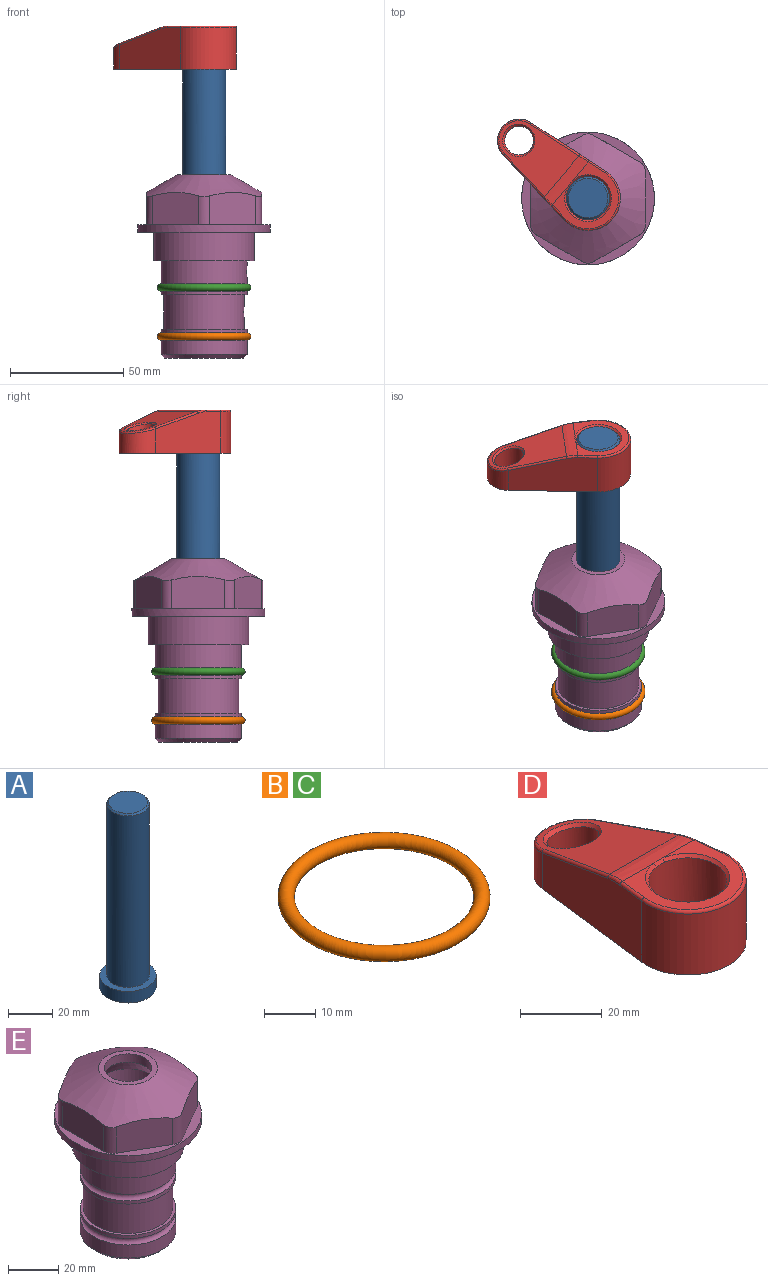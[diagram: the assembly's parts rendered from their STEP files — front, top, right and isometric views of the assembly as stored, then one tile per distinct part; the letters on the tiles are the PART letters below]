
ASSEMBLY  parts=5 mates=4
PART A: 6 faces, bbox 25.4x25.4x101.6 mm
  f0: plane 17.46x17.46mm, normal (0,0,1), area 239.5mm2, adj f5
  f1: plane 25.4x25.4mm, normal (0,0,-1), area 506.7mm2, adj f2
  f2: cylinder r=12.7mm len=25.4mm, axis (0,0,1), area 506.7mm2, adj f1,f3
  f3: plane 25.4x25.4mm, normal (0,0,1), area 221.7mm2, adj f2,f4
  f4: cylinder r=9.53mm len=94.46mm, axis (0,0,1), area 5653mm2, adj f3,f5
  f5: cone r=8.73mm half-angle=45deg, axis (0,0,-1), area 64.4mm2, adj f0,f4
PART B: 1 faces, bbox 44.7x44.7x3.2 mm
  f0: torus R=19.05mm, axis (0,0,1), area 1193.9mm2
PART C: same geometry as B
PART D: 31 faces, bbox 31.7x65.5x19.8 mm
  f0: plane 39.12x18.26mm, normal (0.99,0.12,0), area 612.2mm2, adj f1,f4,f7,f11,f13,f15
  f1: cylinder r=9.53mm len=18.91mm, axis (0,0,-1), area 296.1mm2, adj f0,f2,f7,f17
  f2: plane 39.12x18.26mm, normal (-0.99,0.12,0), area 612.2mm2, adj f1,f4,f7,f12,f14,f16
  f3: cylinder r=6.35mm len=12.7mm, axis (0,0,-1), area 362.4mm2, adj f7,f18
  f4: cylinder r=14.29mm len=28.58mm, axis (0,0,-1), area 882.2mm2, adj f0,f2,f7,f10
  f5: cylinder r=9.53mm len=19.05mm, axis (0,0,-1), area 1092.6mm2, adj f7,f19,f20
  f6: plane 26.99x23.69mm, normal (0,0,1), area 216.2mm2, adj f9,f10,f11,f12,f19
  f7: plane 63.5x28.58mm, normal (0,0,-1), area 661.8mm2, adj f0,f1,f2,f3,f4,f5,f22,f23
  f8: plane 33.52x23.6mm, normal (0,0.26,0.97), area 486mm2, adj f9,f15,f16,f17,f18
  f9: cylinder r=19.05mm len=24.72mm, axis (1,0,0), area 120.4mm2, adj f6,f8,f13,f14,f20
  f10: torus R=13.49mm, axis (0,0,1), area 59mm2, adj f4,f6,f11,f12
  f11: cylinder r=0.79mm len=8.67mm, axis (0.12,-0.99,0), area 10.8mm2, adj f0,f6,f10,f13
  f12: cylinder r=0.79mm len=8.67mm, axis (0.12,0.99,0), area 10.8mm2, adj f2,f6,f10,f14
  f13: bspline ~4.95x1.42mm, area 6.1mm2, adj f0,f9,f11,f15
  f14: bspline ~4.95x1.42mm, area 6.1mm2, adj f2,f9,f12,f16
  f15: cylinder r=0.79mm len=25.95mm, axis (0.12,-0.96,0.26), area 32.9mm2, adj f0,f8,f13,f17
  f16: cylinder r=0.79mm len=25.95mm, axis (0.12,0.96,-0.26), area 32.9mm2, adj f2,f8,f14,f17
  f17: bspline ~18.91x8.38mm, area 30mm2, adj f1,f8,f15,f16
  f18: bspline ~14.29x14.29mm, area 48.3mm2, adj f3,f8
  f19: cone r=9.53mm half-angle=45deg, axis (0,0,1), area 66.5mm2, adj f5,f6,f20
  f20: bspline ~3.22x0.96mm, area 3.5mm2, adj f5,f9,f19
  f21: plane 2.75x2.72mm, normal (0,0,-1), area 2.9mm2, adj f23,f25,f28
  f22: plane 23.05x15.88mm, normal (-0.99,-0.12,0), area 323.6mm2, adj f7,f25,f26,f27,f28,f29
  f23: plane 23.05x15.88mm, normal (0.99,-0.12,0), area 323.6mm2, adj f7,f21,f25,f27,f28,f30
  f24: cylinder r=9.53mm len=10.69mm, axis (0,0,-1), area 114.7mm2, adj f7,f27,f29,f30
  f25: cylinder r=12.7mm len=20.59mm, axis (0,0,-1), area 381.1mm2, adj f7,f21,f22,f23,f26,f28
  f26: plane 2.75x2.72mm, normal (0,0,-1), area 2.9mm2, adj f22,f25,f28
  f27: plane 19.72x18.37mm, normal (0,-0.26,-0.97), area 291.8mm2, adj f22,f23,f24,f28,f29,f30
  f28: cylinder r=15.88mm len=19.92mm, axis (1,0,0), area 54.8mm2, adj f21,f22,f23,f25,f26,f27
  f29: cylinder r=1.59mm len=11mm, axis (0,0,-1), area 34.7mm2, adj f7,f22,f24,f27
  f30: cylinder r=1.59mm len=11mm, axis (0,0,-1), area 34.7mm2, adj f7,f23,f24,f27
PART E: 36 faces, bbox 58.7x58.7x81 mm
  f0: cylinder r=17.78mm len=35.56mm, axis (0,0,1), area 1670.8mm2, adj f23,f24,f31
  f1: cylinder r=19.05mm len=38.1mm, axis (0,0,1), area 1191.9mm2, adj f26,f27,f30
  f2: plane 58.66x58.66mm, normal (0,0,-1), area 1150.6mm2, adj f3,f28
  f3: cylinder r=29.33mm len=58.66mm, axis (0,0,-1), area 585.1mm2, adj f2,f4
  f4: plane 58.66x58.66mm, normal (0,0,1), area 475.9mm2, adj f3,f5,f6,f7,f8,f9,f10,f11
  f5: plane 20.32x14.34mm, normal (-0.5,0.87,0), area 324.4mm2, adj f4,f15,f16,f17
  f6: plane 20.32x14.34mm, normal (0.5,0.87,0), area 324.4mm2, adj f4,f14,f15,f17
  f7: plane 23.48x14.34mm, normal (1,0,0), area 324.4mm2, adj f4,f13,f14,f17
  f8: plane 20.32x14.34mm, normal (0.5,-0.87,0), area 324.4mm2, adj f4,f12,f13,f17
  f9: plane 20.32x14.34mm, normal (-0.5,-0.87,0), area 324.4mm2, adj f4,f11,f12,f17
  f10: plane 23.48x14.34mm, normal (-1,0,0), area 324.4mm2, adj f4,f11,f16,f17
  f11: cylinder r=5.08mm len=12.85mm, axis (0,0,-1), area 67.2mm2, adj f4,f9,f10,f17
  f12: cylinder r=5.08mm len=12.85mm, axis (0,0,-1), area 67.2mm2, adj f4,f8,f9,f17
  f13: cylinder r=5.08mm len=12.85mm, axis (0,0,-1), area 67.2mm2, adj f4,f7,f8,f17
  f14: cylinder r=5.08mm len=12.85mm, axis (0,0,-1), area 67.2mm2, adj f4,f6,f7,f17
  f15: cylinder r=5.08mm len=12.85mm, axis (0,0,-1), area 67.2mm2, adj f4,f5,f6,f17
  f16: cylinder r=5.08mm len=12.85mm, axis (0,0,-1), area 67.2mm2, adj f4,f5,f10,f17
  f17: cone r=11.73mm half-angle=60deg, axis (0,0,-1), area 2071.8mm2, adj f5,f6,f7,f8,f9,f10,f11,f12
  f18: plane 23.46x23.46mm, normal (0,0,1), area 147.4mm2, adj f17,f35
  f19: plane 34.93x34.93mm, normal (0,0,-1), area 958mm2, adj f29
  f20: cylinder r=19.05mm len=38.1mm, axis (0,0,1), area 760.1mm2, adj f21,f29
  f21: torus R=19.05mm, axis (0,0,1), area 565.3mm2, adj f20,f22
  f22: cylinder r=19.05mm len=38.1mm, axis (0,0,1), area 190mm2, adj f21,f23
  f23: plane 38.1x38.1mm, normal (0,0,1), area 146.9mm2, adj f0,f22
  f24: plane 38.1x38.1mm, normal (0,0,-1), area 146.9mm2, adj f0,f25
  f25: cylinder r=19.05mm len=38.1mm, axis (0,0,1), area 190mm2, adj f24,f26
  f26: torus R=19.05mm, axis (0,0,1), area 565.3mm2, adj f1,f25
  f27: plane 44.45x44.45mm, normal (0,0,-1), area 411.7mm2, adj f1,f28
  f28: cylinder r=22.23mm len=44.45mm, axis (0,0,1), area 1773.5mm2, adj f2,f27
  f29: cone r=19.05mm half-angle=45deg, axis (0,0,1), area 257.5mm2, adj f19,f20
  f30: cylinder r=3.17mm len=6.75mm, axis (-1,0,0), area 128mm2, adj f1,f33
  f31: cylinder r=3.17mm len=6.35mm, axis (-1,0,0), area 102.5mm2, adj f0,f33
  f32: plane 25.4x25.4mm, normal (0,0,1), area 506.7mm2, adj f33
  f33: cylinder r=12.7mm len=66.42mm, axis (0,0,-1), area 5236.2mm2, adj f30,f31,f32,f34
  f34: cone r=9.53mm half-angle=30deg, axis (0,0,-1), area 443.4mm2, adj f33,f35
  f35: cylinder r=9.53mm len=19.05mm, axis (0,0,-1), area 240.9mm2, adj f18,f34
PLACE A rot(axis=(0,0,1),50.1deg) t=(0,0,78.42)mm
PLACE B rot(axis=(0,0,1),0deg) t=(0,0,29.27)mm
PLACE C rot(axis=(0,0,1),0deg) t=(0,0,50.86)mm
PLACE D rot(axis=(0,0,1),50.1deg) t=(0,0,78.42)mm
PLACE E rot(axis=(0,0,1),0deg) t=(0,0,50.86)mm fixed
MATE fastened A.f2 <-> D.f4  axis (0,0,1) through (0,0,141.92)mm
MATE fastened C.f0 <-> E.f0  axis (0,0,1) through (0,0,26.35)mm
MATE cylindrical E.f0 <-> A.f2  axis (0,0,1) through (0,0,0.32)mm
MATE fastened B.f0 <-> E.f0  axis (0,0,1) through (0,0,4.76)mm
